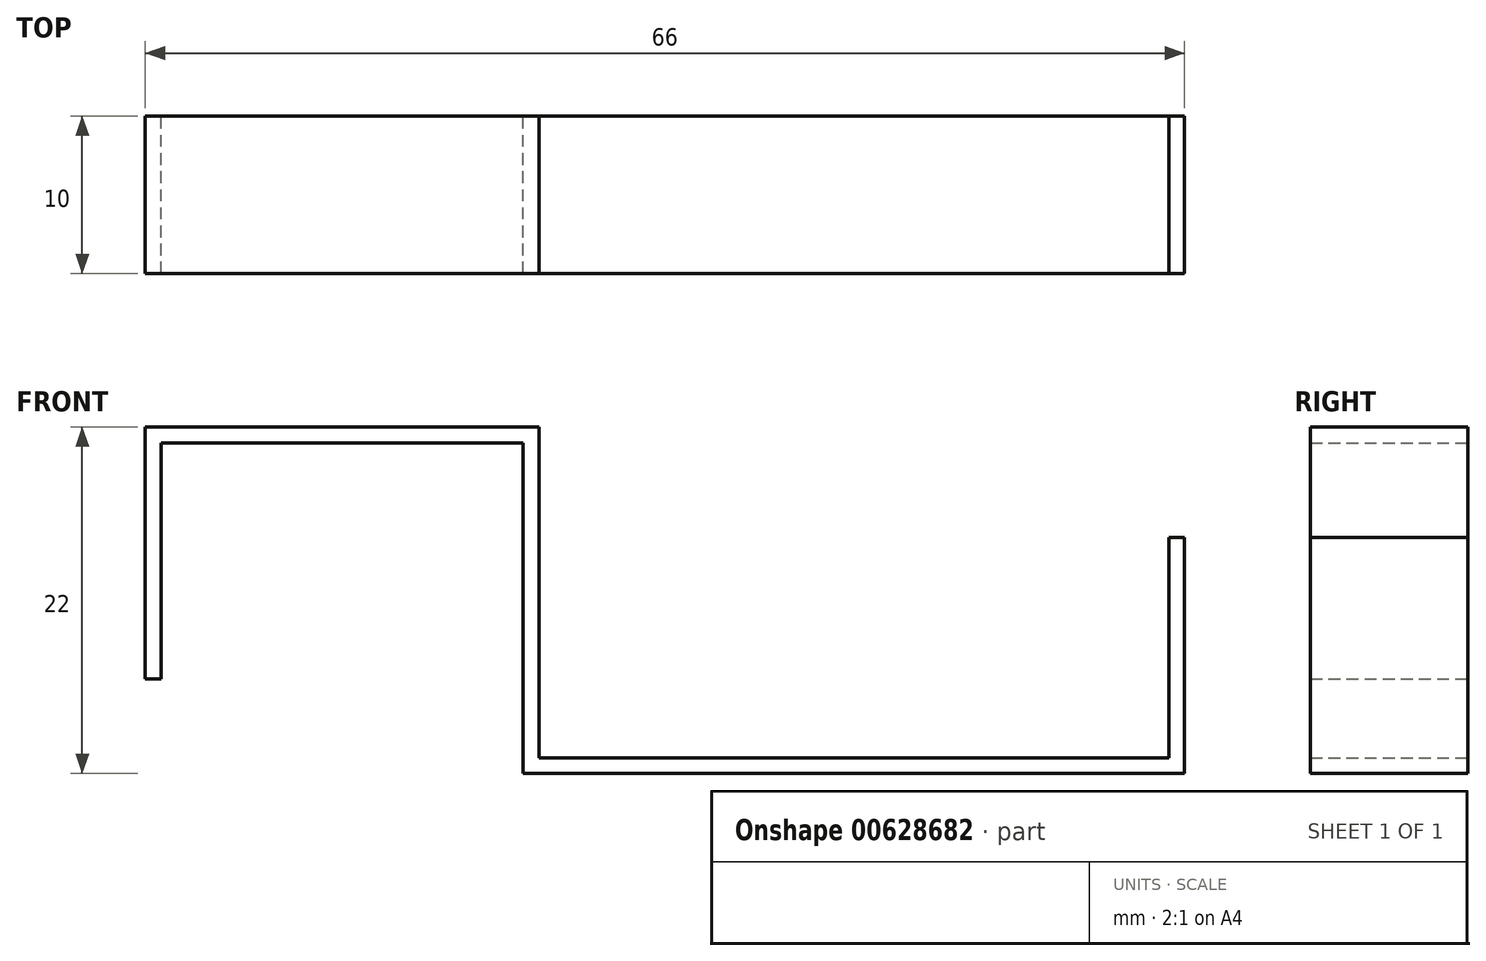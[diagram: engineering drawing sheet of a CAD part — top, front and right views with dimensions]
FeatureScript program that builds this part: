
annotation { "Feature Type Name" : "Feature", "Feature Type Description" : "" }
export const myFeature = defineFeature(function(context is Context, id is Id, definition is map)
    precondition{}
    {
        {
            var Q0;
            Q0=qCreatedBy(makeId("Front.planeOp"),FACE);
            var sketch = newSketch(context, id + "F0", { "sketchPlane" : qUnion([Q0])});
            skLineSegment(sketch, "E0", {"start": v(0, 0) * mm, "end": v(0, 16) * mm});
            skLineSegment(sketch, "E1", {"start": v(0, 16) * mm, "end": v(25, 16) * mm});
            skLineSegment(sketch, "E2", {"start": v(25, 16) * mm, "end": v(25, -5) * mm});
            skLineSegment(sketch, "E3", {"start": v(25, -5) * mm, "end": v(65, -5) * mm});
            skLineSegment(sketch, "E4", {"start": v(65, -5) * mm, "end": v(65, 9) * mm});
            skLineSegment(sketch, "E5", {"start": v(65, 9) * mm, "end": v(66, 9) * mm});
            skLineSegment(sketch, "E6", {"start": v(66, 9) * mm, "end": v(66, -6) * mm});
            skLineSegment(sketch, "E7", {"start": v(66, -6) * mm, "end": v(24, -6) * mm});
            skLineSegment(sketch, "E8", {"start": v(24, -6) * mm, "end": v(24, 15) * mm});
            skLineSegment(sketch, "E9", {"start": v(24, 15) * mm, "end": v(1, 15) * mm});
            skLineSegment(sketch, "E10", {"start": v(1, 15) * mm, "end": v(1, 0) * mm});
            skLineSegment(sketch, "E11", {"start": v(1, 0) * mm, "end": v(0, 0) * mm});
            skSolve(sketch);
        }
        {
            var Q0;
            Q0=makeQuery(id+"F0.imprint","IMPRINT",FACE,{"disambiguationData":[TD([[makeQuery(id+"F0.imprint","IMPRINT",EDGE,{"derivedFrom":sQuery(id+"F0.wireOp",EDGE,"E0")}),-1.0]])]});
            extrude(context, id + "F1", {"entities" : qUnion([Q0]), "depth" : 10 * mm, "offsetDistance" : 25 * mm});
        }
    });
